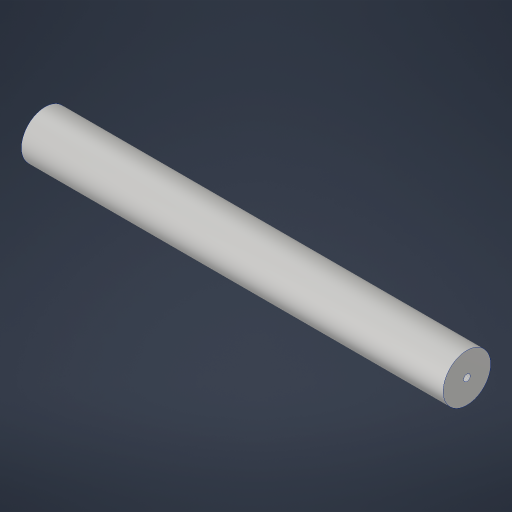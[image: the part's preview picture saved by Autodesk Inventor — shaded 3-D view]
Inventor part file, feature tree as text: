
AUTODESK INVENTOR PART (.ipt)
format: ipt  version: 2023.4 (Build 274418000, 418)  size: 183,808 bytes
history: native  units: in
note: dims shown in document units (in); Inventor stores cm internally (conversion verified against a paired STEP export)
features: sketch x4, hole x2, extrude x1
ambient origin geometry x8: Origin, YZ Plane, XZ Plane, XY Plane, X Axis, Y Axis, Z Axis, Center Point
bodies: Solid1 (feature_tree)
feature tree (7):
  sketch  "Sketch1"  dims[d0=1.125in d1=10.0in d2=0.0in]
  extrude  "Extrusion1"  Depth=10.0in TaperAngle=0.0deg
  sketch  "Sketch3"  dims[d10=0.156in d11=0.38in d12=0.375in d13=0.25in d14=0.5635in d15=0.536in d16=0.8108in]
  sketch  "Sketch4"
  hole  "Hole1"  [1 undecoded]
  hole  "Hole2"  [1 undecoded]
  sketch  "Sketch2"  dims[d3=0.156in d4=0.38in d5=0.385in d6=0.25in d7=0.5635in d8=0.536in d9=0.8108in]
note: 2 required parameter values undecoded (feature->parameter linkage not recoverable at this tier; creation-order binding heuristic only, values carry confidence <= 0.55)
